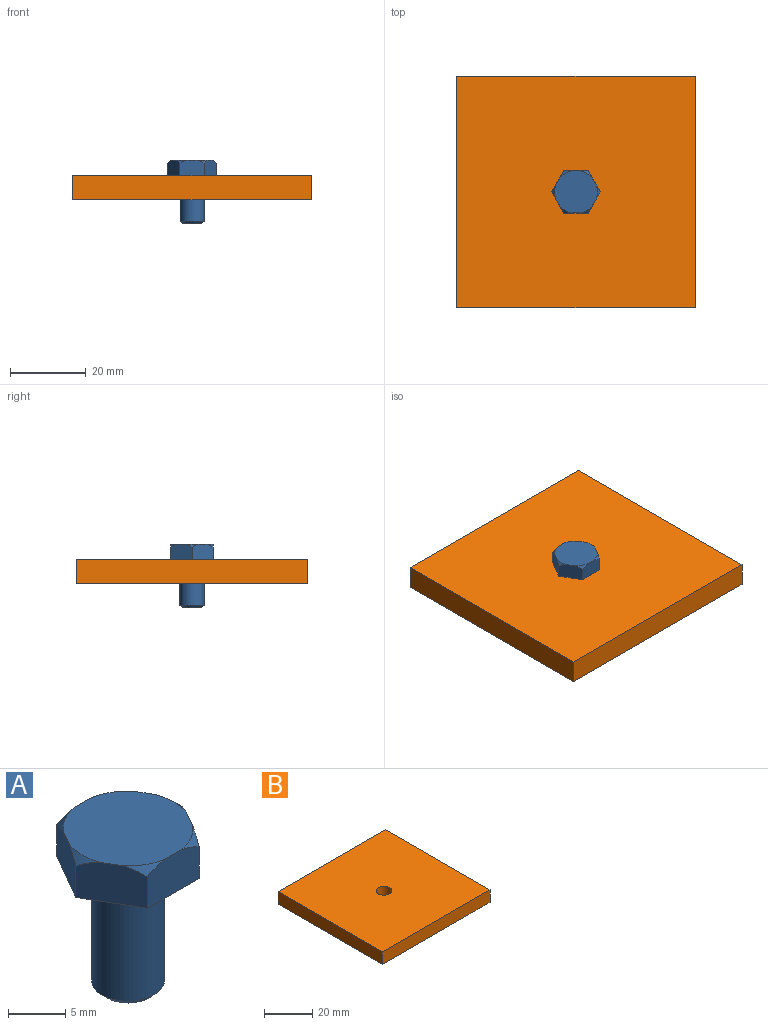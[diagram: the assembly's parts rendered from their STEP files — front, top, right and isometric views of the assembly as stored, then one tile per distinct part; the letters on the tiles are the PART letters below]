
ASSEMBLY  parts=2 mates=1
PART A: 18 faces, bbox 12.9x12.6x16.8 mm
  f0: plane 5.08x5.08mm, normal (0,0,-1), area 20.3mm2, adj f17
  f1: cylinder r=3.17mm len=11.75mm, axis (0,0,-1), area 234.4mm2, adj f16,f17
  f2: plane 12.85x11.13mm, normal (0,0,-1), area 68.9mm2, adj f3,f4,f5,f6,f7,f8,f16
  f3: plane 5.57x4.14mm, normal (0.87,0.5,0), area 25.2mm2, adj f2,f4,f6,f9,f13,f15
  f4: plane 6.43x4.14mm, normal (0,1,0), area 25.2mm2, adj f2,f3,f5,f9,f14,f15
  f5: plane 5.57x4.14mm, normal (-0.87,0.5,0), area 25.2mm2, adj f2,f4,f7,f9,f12,f14
  f6: plane 5.57x4.14mm, normal (0.87,-0.5,0), area 25.2mm2, adj f2,f3,f8,f9,f11,f13
  f7: plane 5.57x4.14mm, normal (-0.87,-0.5,0), area 25.2mm2, adj f2,f5,f8,f9,f10,f12
  f8: plane 6.43x4.14mm, normal (0,-1,0), area 25.2mm2, adj f2,f6,f7,f9,f10,f11
  f9: plane 11.32x11.13mm, normal (0,0,1), area 99.9mm2, adj f3,f4,f5,f6,f7,f8,f10,f11
  f10: cone r=5.66mm half-angle=45deg, axis (0,0,-1), area 1.7mm2, adj f7,f8,f9
  f11: cone r=5.66mm half-angle=45deg, axis (0,0,-1), area 1.7mm2, adj f6,f8,f9
  f12: cone r=5.66mm half-angle=45deg, axis (0,0,-1), area 1.7mm2, adj f5,f7,f9
  f13: cone r=5.66mm half-angle=45deg, axis (0,0,-1), area 1.7mm2, adj f3,f6,f9
  f14: cone r=5.66mm half-angle=45deg, axis (0,0,-1), area 1.7mm2, adj f4,f5,f9
  f15: cone r=5.66mm half-angle=45deg, axis (0,0,-1), area 1.7mm2, adj f3,f4,f9
  f16: torus R=3.49mm, axis (0,0,1), area 10.3mm2, adj f1,f2
  f17: cone r=2.54mm half-angle=45deg, axis (0,0,1), area 16.1mm2, adj f0,f1
PART B: 7 faces, bbox 63x61.1x6.4 mm
  f0: plane 61.14x6.35mm, normal (1,0,0), area 388.2mm2, adj f1,f4,f5,f6
  f1: plane 62.96x6.35mm, normal (0,1,0), area 399.8mm2, adj f0,f2,f5,f6
  f2: plane 61.14x6.35mm, normal (-1,0,0), area 388.2mm2, adj f1,f4,f5,f6
  f3: cylinder r=3.17mm len=6.35mm, axis (0,0,1), area 126.7mm2, adj f5,f6
  f4: plane 62.96x6.35mm, normal (0,-1,0), area 399.8mm2, adj f0,f2,f5,f6
  f5: plane 62.96x61.14mm, normal (0,0,-1), area 3817.4mm2, adj f0,f1,f2,f3,f4
  f6: plane 62.96x61.14mm, normal (0,0,1), area 3817.4mm2, adj f0,f1,f2,f3,f4
PLACE A t=(-21.54,3.43,12.2)mm
PLACE B t=(-21.54,3.43,37.6)mm fixed
MATE revolute B.f3 <-> A.f1  axis (0,0,1) through (-21.54,3.43,37.6)mm
